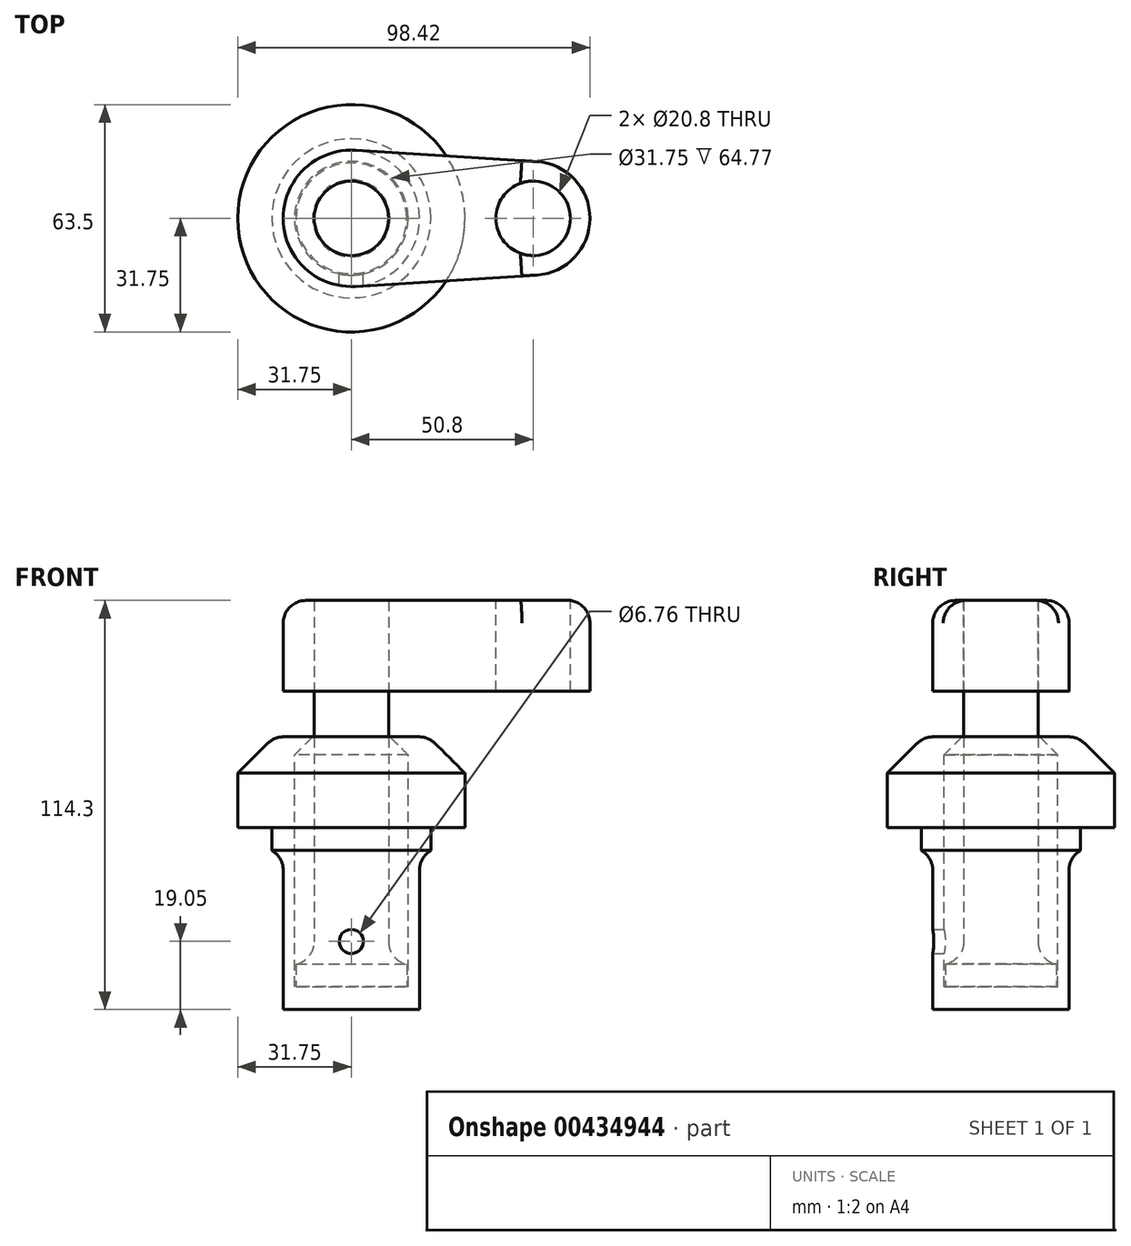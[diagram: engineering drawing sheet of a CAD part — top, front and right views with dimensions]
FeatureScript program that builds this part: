
annotation { "Feature Type Name" : "Feature", "Feature Type Description" : "" }
export const myFeature = defineFeature(function(context is Context, id is Id, definition is map)
    precondition{}
    {
        {
            var Q0;
            Q0=qCreatedBy(makeId("Front.planeOp"),FACE);
            var sketch = newSketch(context, id + "F0", { "sketchPlane" : qUnion([Q0])});
            skLineSegment(sketch, "E0", {"start": v(0, 0) * mm, "end": v(0, 76.2) * mm});
            skLineSegment(sketch, "E1", {"start": v(0, 76.2) * mm, "end": v(21.6, 76.2) * mm});
            skLineSegment(sketch, "E2", {"start": v(21.59, 76.2) * mm, "end": v(31.75, 66.04) * mm});
            skLineSegment(sketch, "E3", {"start": v(31.75, 66.04) * mm, "end": v(31.75, 50.8) * mm});
            skLineSegment(sketch, "E4", {"start": v(31.75, 50.8) * mm, "end": v(22.23, 50.8) * mm});
            skLineSegment(sketch, "E5", {"start": v(22.23, 50.8) * mm, "end": v(22.23, 44.45) * mm});
            skLineSegment(sketch, "E6", {"start": v(22.23, 44.45) * mm, "end": v(19.05, 44.45) * mm});
            skLineSegment(sketch, "E7", {"start": v(19.05, 44.45) * mm, "end": v(19.05, 0) * mm});
            skLineSegment(sketch, "E8", {"start": v(19.05, 0) * mm, "end": v(0, 0) * mm});
            skLineSegment(sketch, "E9", {"start": v(10.8, 76.2) * mm, "end": v(15.88, 71.12) * mm});
            skLineSegment(sketch, "E10", {"start": v(15.88, 71.12) * mm, "end": v(15.88, 6.35) * mm});
            skLineSegment(sketch, "E11", {"start": v(15.88, 6.35) * mm, "end": v(0, 6.35) * mm});
            skLineSegment(sketch, "E12", {"start": v(0, 76.2) * mm, "end": v(0, 91.38) * mm, "construction": true});
            skLineSegment(sketch, "E13", {"start": v(0, 76.2) * mm, "end": v(0, 114.3) * mm});
            skLineSegment(sketch, "E14", {"start": v(0, 114.3) * mm, "end": v(10.4, 114.3) * mm});
            skLineSegment(sketch, "E15", {"start": v(10.4, 114.3) * mm, "end": v(10.4, 12.7) * mm});
            skLineSegment(sketch, "E16", {"start": v(10.4, 12.7) * mm, "end": v(15.48, 12.7) * mm});
            skLineSegment(sketch, "E17", {"start": v(15.48, 12.7) * mm, "end": v(15.48, 6.35) * mm});
            skSolve(sketch);
        }
        {
            var Q0;
            {var subQ4=sQuery(id+"F0.wireOp",EDGE,"E2");Q0=makeQuery(id+"F0.imprint","IMPRINT",FACE,{"disambiguationData":[TD([[makeQuery(id+"F0.imprint","IMPRINT",EDGE,{"derivedFrom":subQ4}),-1.0]])]});}
            var Q1;
            Q1=sQuery(id+"F0.wireOp",EDGE,"E0");
            revolve(context, id + "F1", {"entities" : qUnion([Q0]), "axis" : qUnion([Q1]), "revolveType" : RevolveType.FULL, "oppositeDirection" : true});
        }
        {
            var Q0;
            {var subQ0=sQuery(id+"F0.wireOp",EDGE,"E13");Q0=makeQuery(id+"F0.imprint","IMPRINT",FACE,{"disambiguationData":[TD([[makeQuery(id+"F0.imprint","IMPRINT",EDGE,{"derivedFrom":subQ0}),-1.0]])]});}
            var Q1;
            {var subQ0=sQuery(id+"F0.wireOp",EDGE,"E16");Q1=makeQuery(id+"F0.imprint","IMPRINT",FACE,{"disambiguationData":[TD([[makeQuery(id+"F0.imprint","IMPRINT",EDGE,{"derivedFrom":subQ0}),-1.0]])]});}
            var Q2;
            Q2=sQuery(id+"F0.wireOp",EDGE,"E13");
            revolve(context, id + "F2", {"entities" : qUnion([Q0, Q1]), "axis" : qUnion([Q2]), "revolveType" : RevolveType.FULL});
        }
        {
            var Q0;
            Q0=makeQuery(id+"F2.opRevolve","SWEPT_FACE",FACE,{"disambiguationData":[OSD([sQuery(id+"F0.wireOp",EDGE,"E14")])]});
            var sketch = newSketch(context, id + "F3", { "sketchPlane" : qUnion([Q0])});
            skCircle(sketch, "E18", {"center": v(0, 0) * mm, "radius": 19.05 * mm});
            skCircle(sketch, "E19", {"center": v(50.8, 0) * mm, "radius": 15.88 * mm});
            skLineSegment(sketch, "E20", {"start": v(51.8, 15.84) * mm, "end": v(1.2, 19.01) * mm});
            skLineSegment(sketch, "E21", {"start": v(1.2, -19.01) * mm, "end": v(51.8, -15.84) * mm});
            skCircle(sketch, "E22.0", {"center": v(0, 0) * mm, "radius": 10.4 * mm});
            skCircle(sketch, "E23", {"center": v(50.8, 0) * mm, "radius": 10.4 * mm});
            skSolve(sketch);
        }
        {
            var Q0;
            {var subQ0=sQuery(id+"F3.wireOp",EDGE,"E20");Q0=makeQuery(id+"F3.imprint","IMPRINT",FACE,{"disambiguationData":[TD([[makeQuery(id+"F3.imprint","IMPRINT",EDGE,{"derivedFrom":subQ0}),1.0]])]});}
            var Q1;
            Q1=makeQuery(id+"F3.imprint","IMPRINT",FACE,{"disambiguationData":[TD([[makeQuery(id+"F3.imprint","IMPRINT",EDGE,{"derivedFrom":sQuery(id+"F3.wireOp",EDGE,"E23")}),-1.0]])]});
            var Q2;
            Q2=makeQuery(id+"F3.imprint","IMPRINT",FACE,{"disambiguationData":[TD([[makeQuery(id+"F3.imprint","IMPRINT",EDGE,{"derivedFrom":sQuery(id+"F3.wireOp",EDGE,"E22.0")}),1.0]])]});
            var Q3;
            Q3=makeQuery(id+"F1.opRevolve","SWEPT_FACE",FACE,{"disambiguationData":[OSD([sQuery(id+"F0.wireOp",EDGE,"E1")])]});
            extrude(context, id + "F4", {"entities" : qUnion([Q0, Q1, Q2]), "oppositeDirection" : true, "endBoundEntityFace" : qUnion([Q3]), "depth" : 25.4 * mm});
        }
        {
            var Q0;
            Q0=qCreatedBy(makeId("Front.planeOp"),FACE);
            var sketch = newSketch(context, id + "F5", { "sketchPlane" : qUnion([Q0])});
            skPoint(sketch, "E24", {"position": v(0, 19.05) * mm});
            skSolve(sketch);
        }
        {
            var Q0;
            Q0=sQuery(id+"F5.wireOp",VERTEX,"E24");
            var Q1;
            Q1=makeQuery(id+"F1.opRevolve","SWEPT_BODY",BODY,{"disambiguationData":[OSD([sQuery(id+"F0.wireOp",EDGE,"E0"),sQuery(id+"F0.wireOp",EDGE,"E1"),sQuery(id+"F0.wireOp",EDGE,"E2"),sQuery(id+"F0.wireOp",EDGE,"E3"),sQuery(id+"F0.wireOp",EDGE,"E4"),sQuery(id+"F0.wireOp",EDGE,"E5"),sQuery(id+"F0.wireOp",EDGE,"E6"),sQuery(id+"F0.wireOp",EDGE,"E7"),sQuery(id+"F0.wireOp",EDGE,"E8"),sQuery(id+"F0.wireOp",EDGE,"E9"),sQuery(id+"F0.wireOp",EDGE,"E10"),sQuery(id+"F0.wireOp",EDGE,"E11")])]});
            hole(context, id + "F6", {"style" : HoleStyle.SIMPLE, "endStyle" : HoleEndStyle.THROUGH, "oppositeDirection" : true, "standardTappedOrClearance" : lookupTablePath({ "standard" : "ANSI", "fit" : "Normal (ASME)", "size" : "1/4", "type" : "Clearance" }), "standardBlindInLast" : lookupTablePath({ "fit" : "Free", "standard" : "ANSI", "size" : "1/4", "type" : "Clearance" }), "holeDiameter" : 6.76 * mm, "isTappedThrough" : true, "tappedDepth" : 8.9 * mm, "tapClearance" : 3, "locations" : qUnion([Q0]), "scope" : qUnion([Q1])});
        }
        {
            var Q0;
            Q0=makeQuery(id+"F4.opExtrude","CAP_EDGE",EDGE,{"disambiguationData":[OSD([sQuery(id+"F3.wireOp",EDGE,"E20")])],"isStart":true});
            var Q1;
            Q1=makeQuery(id+"F1.opRevolve","SWEPT_EDGE",EDGE,{"disambiguationData":[OSD([sQuery(id+"F0.wireOp",EDGE,"E1"),sQuery(id+"F0.wireOp",EDGE,"E2")])]});
            var Q2;
            Q2=makeQuery(id+"F1.opRevolve","SWEPT_EDGE",EDGE,{"disambiguationData":[OSD([sQuery(id+"F0.wireOp",EDGE,"E6"),sQuery(id+"F0.wireOp",EDGE,"E7")])]});
            var Q3;
            Q3=makeQuery(id+"F2.opRevolve","SWEPT_EDGE",EDGE,{"disambiguationData":[OSD([sQuery(id+"F0.wireOp",EDGE,"E15"),sQuery(id+"F0.wireOp",EDGE,"E16")])]});
            fillet(context, id + "F7", {"entities" : qUnion([Q0, Q1, Q2, Q3]), "radius" : 6.35 * mm, "tangentPropagation" : true, "allowEdgeOverflow" : false});
        }
    });
